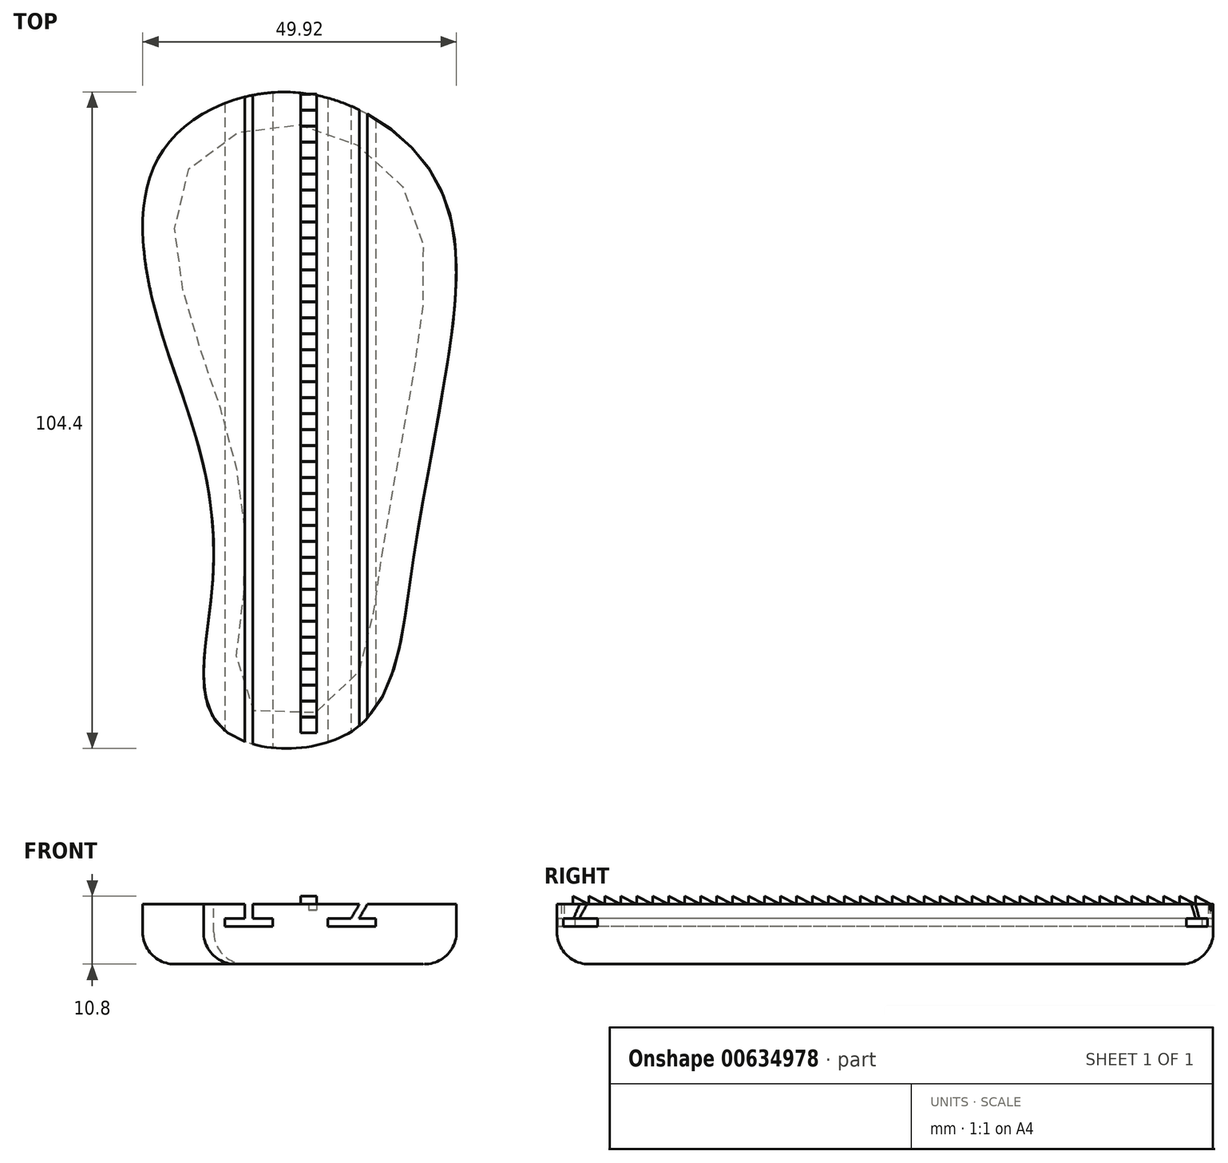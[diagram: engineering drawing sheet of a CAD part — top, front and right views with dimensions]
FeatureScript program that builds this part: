
annotation { "Feature Type Name" : "Feature", "Feature Type Description" : "" }
export const myFeature = defineFeature(function(context is Context, id is Id, definition is map)
    precondition{}
    {
        {
            var Q0;
            Q0=qCreatedBy(makeId("Top.planeOp"),FACE);
            var sketch = newSketch(context, id + "F0", { "sketchPlane" : qUnion([Q0])});
            skFitSpline(sketch, "E0", {"points": [v(-19.82, 9.13) * mm, v(-18.34, 32.17) * mm, v(3.23, 41.76) * mm, v(25.53, 27.56) * mm, v(27.38, 0) * mm, v(21.48, -34.38) * mm, v(12.26, -59.64) * mm, v(-9.13, -58.9) * mm, v(-10.23, -37.15) * mm, v(-12.63, -13.73) * mm, v(-19.82, 9.13) * mm]});
            skSolve(sketch);
        }
        {
            var Q0;
            Q0=makeQuery(id+"F0.imprint","IMPRINT",FACE,{"disambiguationData":[TD([[makeQuery(id+"F0.imprint","IMPRINT",EDGE,{"derivedFrom":sQuery(id+"F0.wireOp",EDGE,"E0")}),-1.0]])]});
            extrude(context, id + "F1", {"entities" : qUnion([Q0]), "depth" : 9.52 * mm, "offsetDistance" : 25.4 * mm});
        }
        {
            var Q0;
            Q0=makeQuery(id+"F1.opExtrude","CAP_EDGE",EDGE,{"disambiguationData":[OSD([sQuery(id+"F0.wireOp",EDGE,"E0")])],"isStart":true});
            fillet(context, id + "F2", {"entities" : qUnion([Q0]), "radius" : 5.08 * mm, "tangentPropagation" : true, "allowEdgeOverflow" : false});
        }
        {
            var Q0;
            Q0=qCreatedBy(makeId("Front.planeOp"),FACE);
            var sketch = newSketch(context, id + "F3", { "sketchPlane" : qUnion([Q0])});
            skLineSegment(sketch, "E1.bottom", {"start": v(8.16, 7.27) * mm, "end": v(11.85, 7.27) * mm});
            skLineSegment(sketch, "E1.top", {"start": v(8.16, 6) * mm, "end": v(15.78, 6) * mm});
            skLineSegment(sketch, "E1.left", {"start": v(8.16, 7.27) * mm, "end": v(8.16, 6) * mm});
            skLineSegment(sketch, "E1.right", {"start": v(15.78, 7.27) * mm, "end": v(15.78, 6) * mm});
            skLineSegment(sketch, "E2.bottom", {"start": v(15.73, 13.84) * mm, "end": v(17, 13.84) * mm});
            skLineSegment(sketch, "E2.left", {"start": v(15.73, 13.84) * mm, "end": v(11.85, 7.27) * mm});
            skLineSegment(sketch, "E2.right", {"start": v(17, 13.84) * mm, "end": v(13.12, 7.27) * mm});
            skLineSegment(sketch, "E3.bottom", {"start": v(-8.2, 6) * mm, "end": v(-0.59, 6) * mm});
            skLineSegment(sketch, "E3.top", {"start": v(-8.2, 7.27) * mm, "end": v(-5.06, 7.27) * mm});
            skLineSegment(sketch, "E3.left", {"start": v(-8.2, 6) * mm, "end": v(-8.2, 7.27) * mm});
            skLineSegment(sketch, "E3.right", {"start": v(-0.59, 6) * mm, "end": v(-0.59, 7.27) * mm});
            skLineSegment(sketch, "E4.bottom", {"start": v(-5.06, 13.84) * mm, "end": v(-3.79, 13.84) * mm});
            skLineSegment(sketch, "E4.left", {"start": v(-5.06, 13.84) * mm, "end": v(-5.06, 7.27) * mm});
            skLineSegment(sketch, "E4.right", {"start": v(-3.79, 13.84) * mm, "end": v(-3.79, 7.27) * mm});
            skLineSegment(sketch, "E5.trimOffspring", {"start": v(-3.79, 7.27) * mm, "end": v(-0.59, 7.27) * mm});
            skLineSegment(sketch, "E6.trimOffspring", {"start": v(13.12, 7.27) * mm, "end": v(15.78, 7.27) * mm});
            skSolve(sketch);
        }
        {
            var Q0;
            Q0=makeQuery(id+"F3.imprint","IMPRINT",FACE,{"disambiguationData":[TD([[makeQuery(id+"F3.imprint","IMPRINT",EDGE,{"derivedFrom":sQuery(id+"F3.wireOp",EDGE,"E3.bottom")}),1.0]])]});
            var Q1;
            Q1=makeQuery(id+"F3.imprint","IMPRINT",FACE,{"disambiguationData":[TD([[makeQuery(id+"F3.imprint","IMPRINT",EDGE,{"derivedFrom":sQuery(id+"F3.wireOp",EDGE,"E1.bottom")}),-1.0]])]});
            extrude(context, id + "F4", {"entities" : qUnion([Q0, Q1]), "operationType" : NewBodyOperationType.REMOVE, "endBound" : BoundingType.THROUGH_ALL, "oppositeDirection" : true, "depth" : 25.4 * mm, "offsetDistance" : 25.4 * mm, "hasSecondDirection" : true, "secondDirectionBound" : SecondDirectionBoundingType.THROUGH_ALL, "secondDirectionOppositeDirection" : false, "secondDirectionDepth" : 25.4 * mm});
        }
        {
            var Q0;
            Q0=qCreatedBy(makeId("Right.planeOp"),FACE);
            cPlane(context, id + "F5", {"entities" : qUnion([Q0]), "cplaneType" : CPlaneType.OFFSET, "offset" : 5.08 * mm, "width" : 152.4 * mm, "height" : 152.4 * mm});
        }
        {
            var Q0;
            Q0=qCreatedBy(id+"F5.planeOp",FACE);
            var sketch = newSketch(context, id + "F6", { "sketchPlane" : qUnion([Q0])});
            skLineSegment(sketch, "E7", {"start": v(41.54, 9.5) * mm, "end": v(39, 10.8) * mm});
            skLineSegment(sketch, "E8", {"start": v(39, 10.8) * mm, "end": v(39, 9.53) * mm});
            skLineSegment(sketch, "E9", {"start": v(41.54, 9.5) * mm, "end": v(41.54, 8.6) * mm});
            skLineSegment(sketch, "E10", {"start": v(41.54, 8.6) * mm, "end": v(38.99, 8.6) * mm});
            skLineSegment(sketch, "E11", {"start": v(38.99, 8.6) * mm, "end": v(39, 9.53) * mm});
            skLineSegment(sketch, "E12.1.0.0", {"start": v(39, 9.5) * mm, "end": v(36.46, 10.8) * mm});
            skLineSegment(sketch, "E12.1.0.1", {"start": v(36.46, 10.8) * mm, "end": v(36.46, 9.53) * mm});
            skLineSegment(sketch, "E12.1.0.2", {"start": v(36.45, 8.6) * mm, "end": v(36.46, 9.53) * mm});
            skLineSegment(sketch, "E12.1.0.3", {"start": v(39, 8.6) * mm, "end": v(36.45, 8.6) * mm});
            skLineSegment(sketch, "E12.1.0.4", {"start": v(39, 9.5) * mm, "end": v(39, 8.6) * mm});
            skLineSegment(sketch, "E12.2.0.0", {"start": v(36.46, 9.5) * mm, "end": v(33.92, 10.8) * mm});
            skLineSegment(sketch, "E12.2.0.1", {"start": v(33.92, 10.8) * mm, "end": v(33.92, 9.53) * mm});
            skLineSegment(sketch, "E12.2.0.2", {"start": v(33.9, 8.6) * mm, "end": v(33.92, 9.53) * mm});
            skLineSegment(sketch, "E12.2.0.3", {"start": v(36.46, 8.6) * mm, "end": v(33.9, 8.6) * mm});
            skLineSegment(sketch, "E12.2.0.4", {"start": v(36.46, 9.5) * mm, "end": v(36.46, 8.6) * mm});
            skLineSegment(sketch, "E12.3.0.0", {"start": v(33.92, 9.5) * mm, "end": v(31.38, 10.8) * mm});
            skLineSegment(sketch, "E12.3.0.1", {"start": v(31.38, 10.8) * mm, "end": v(31.38, 9.53) * mm});
            skLineSegment(sketch, "E12.3.0.2", {"start": v(31.37, 8.6) * mm, "end": v(31.38, 9.53) * mm});
            skLineSegment(sketch, "E12.3.0.3", {"start": v(33.92, 8.6) * mm, "end": v(31.37, 8.6) * mm});
            skLineSegment(sketch, "E12.3.0.4", {"start": v(33.92, 9.5) * mm, "end": v(33.92, 8.6) * mm});
            skLineSegment(sketch, "E12.4.0.0", {"start": v(31.38, 9.5) * mm, "end": v(28.84, 10.8) * mm});
            skLineSegment(sketch, "E12.4.0.1", {"start": v(28.84, 10.8) * mm, "end": v(28.84, 9.53) * mm});
            skLineSegment(sketch, "E12.4.0.2", {"start": v(28.83, 8.6) * mm, "end": v(28.84, 9.53) * mm});
            skLineSegment(sketch, "E12.4.0.3", {"start": v(31.38, 8.6) * mm, "end": v(28.83, 8.6) * mm});
            skLineSegment(sketch, "E12.4.0.4", {"start": v(31.38, 9.5) * mm, "end": v(31.38, 8.6) * mm});
            skLineSegment(sketch, "E12.5.0.0", {"start": v(28.84, 9.5) * mm, "end": v(26.3, 10.8) * mm});
            skLineSegment(sketch, "E12.5.0.1", {"start": v(26.3, 10.8) * mm, "end": v(26.3, 9.53) * mm});
            skLineSegment(sketch, "E12.5.0.2", {"start": v(26.29, 8.6) * mm, "end": v(26.3, 9.53) * mm});
            skLineSegment(sketch, "E12.5.0.3", {"start": v(28.84, 8.6) * mm, "end": v(26.29, 8.6) * mm});
            skLineSegment(sketch, "E12.5.0.4", {"start": v(28.84, 9.5) * mm, "end": v(28.84, 8.6) * mm});
            skLineSegment(sketch, "E12.6.0.0", {"start": v(26.3, 9.5) * mm, "end": v(23.76, 10.8) * mm});
            skLineSegment(sketch, "E12.6.0.1", {"start": v(23.76, 10.8) * mm, "end": v(23.76, 9.53) * mm});
            skLineSegment(sketch, "E12.6.0.2", {"start": v(23.75, 8.6) * mm, "end": v(23.76, 9.53) * mm});
            skLineSegment(sketch, "E12.6.0.3", {"start": v(26.3, 8.6) * mm, "end": v(23.75, 8.6) * mm});
            skLineSegment(sketch, "E12.6.0.4", {"start": v(26.3, 9.5) * mm, "end": v(26.3, 8.6) * mm});
            skLineSegment(sketch, "E12.7.0.0", {"start": v(23.76, 9.5) * mm, "end": v(21.22, 10.8) * mm});
            skLineSegment(sketch, "E12.7.0.1", {"start": v(21.22, 10.8) * mm, "end": v(21.22, 9.53) * mm});
            skLineSegment(sketch, "E12.7.0.2", {"start": v(21.2, 8.6) * mm, "end": v(21.22, 9.53) * mm});
            skLineSegment(sketch, "E12.7.0.3", {"start": v(23.76, 8.6) * mm, "end": v(21.2, 8.6) * mm});
            skLineSegment(sketch, "E12.7.0.4", {"start": v(23.76, 9.5) * mm, "end": v(23.76, 8.6) * mm});
            skLineSegment(sketch, "E12.8.0.0", {"start": v(21.22, 9.5) * mm, "end": v(18.68, 10.8) * mm});
            skLineSegment(sketch, "E12.8.0.1", {"start": v(18.68, 10.8) * mm, "end": v(18.68, 9.53) * mm});
            skLineSegment(sketch, "E12.8.0.2", {"start": v(18.67, 8.6) * mm, "end": v(18.68, 9.53) * mm});
            skLineSegment(sketch, "E12.8.0.3", {"start": v(21.22, 8.6) * mm, "end": v(18.67, 8.6) * mm});
            skLineSegment(sketch, "E12.8.0.4", {"start": v(21.22, 9.5) * mm, "end": v(21.22, 8.6) * mm});
            skLineSegment(sketch, "E12.9.0.0", {"start": v(18.68, 9.5) * mm, "end": v(16.14, 10.8) * mm});
            skLineSegment(sketch, "E12.9.0.1", {"start": v(16.14, 10.8) * mm, "end": v(16.14, 9.53) * mm});
            skLineSegment(sketch, "E12.9.0.2", {"start": v(16.13, 8.6) * mm, "end": v(16.14, 9.53) * mm});
            skLineSegment(sketch, "E12.9.0.3", {"start": v(18.68, 8.6) * mm, "end": v(16.13, 8.6) * mm});
            skLineSegment(sketch, "E12.9.0.4", {"start": v(18.68, 9.5) * mm, "end": v(18.68, 8.6) * mm});
            skLineSegment(sketch, "E12.10.0.0", {"start": v(16.14, 9.5) * mm, "end": v(13.6, 10.8) * mm});
            skLineSegment(sketch, "E12.10.0.1", {"start": v(13.6, 10.8) * mm, "end": v(13.6, 9.53) * mm});
            skLineSegment(sketch, "E12.10.0.2", {"start": v(13.59, 8.6) * mm, "end": v(13.6, 9.53) * mm});
            skLineSegment(sketch, "E12.10.0.3", {"start": v(16.14, 8.6) * mm, "end": v(13.59, 8.6) * mm});
            skLineSegment(sketch, "E12.10.0.4", {"start": v(16.14, 9.5) * mm, "end": v(16.14, 8.6) * mm});
            skLineSegment(sketch, "E12.11.0.0", {"start": v(13.6, 9.5) * mm, "end": v(11.06, 10.8) * mm});
            skLineSegment(sketch, "E12.11.0.1", {"start": v(11.06, 10.8) * mm, "end": v(11.06, 9.53) * mm});
            skLineSegment(sketch, "E12.11.0.2", {"start": v(11.05, 8.6) * mm, "end": v(11.06, 9.53) * mm});
            skLineSegment(sketch, "E12.11.0.3", {"start": v(13.6, 8.6) * mm, "end": v(11.05, 8.6) * mm});
            skLineSegment(sketch, "E12.11.0.4", {"start": v(13.6, 9.5) * mm, "end": v(13.6, 8.6) * mm});
            skLineSegment(sketch, "E12.12.0.0", {"start": v(11.06, 9.5) * mm, "end": v(8.52, 10.8) * mm});
            skLineSegment(sketch, "E12.12.0.1", {"start": v(8.52, 10.8) * mm, "end": v(8.52, 9.53) * mm});
            skLineSegment(sketch, "E12.12.0.2", {"start": v(8.5, 8.6) * mm, "end": v(8.52, 9.53) * mm});
            skLineSegment(sketch, "E12.12.0.3", {"start": v(11.06, 8.6) * mm, "end": v(8.5, 8.6) * mm});
            skLineSegment(sketch, "E12.12.0.4", {"start": v(11.06, 9.5) * mm, "end": v(11.06, 8.6) * mm});
            skLineSegment(sketch, "E12.13.0.0", {"start": v(8.52, 9.5) * mm, "end": v(5.98, 10.8) * mm});
            skLineSegment(sketch, "E12.13.0.1", {"start": v(5.98, 10.8) * mm, "end": v(5.98, 9.53) * mm});
            skLineSegment(sketch, "E12.13.0.2", {"start": v(5.97, 8.6) * mm, "end": v(5.98, 9.53) * mm});
            skLineSegment(sketch, "E12.13.0.3", {"start": v(8.52, 8.6) * mm, "end": v(5.97, 8.6) * mm});
            skLineSegment(sketch, "E12.13.0.4", {"start": v(8.52, 9.5) * mm, "end": v(8.52, 8.6) * mm});
            skLineSegment(sketch, "E12.14.0.0", {"start": v(5.98, 9.5) * mm, "end": v(3.44, 10.8) * mm});
            skLineSegment(sketch, "E12.14.0.1", {"start": v(3.44, 10.8) * mm, "end": v(3.44, 9.53) * mm});
            skLineSegment(sketch, "E12.14.0.2", {"start": v(3.43, 8.6) * mm, "end": v(3.44, 9.53) * mm});
            skLineSegment(sketch, "E12.14.0.3", {"start": v(5.98, 8.6) * mm, "end": v(3.43, 8.6) * mm});
            skLineSegment(sketch, "E12.14.0.4", {"start": v(5.98, 9.5) * mm, "end": v(5.98, 8.6) * mm});
            skLineSegment(sketch, "E12.15.0.0", {"start": v(3.44, 9.5) * mm, "end": v(0.9, 10.8) * mm});
            skLineSegment(sketch, "E12.15.0.1", {"start": v(0.9, 10.8) * mm, "end": v(0.9, 9.53) * mm});
            skLineSegment(sketch, "E12.15.0.2", {"start": v(0.89, 8.6) * mm, "end": v(0.9, 9.53) * mm});
            skLineSegment(sketch, "E12.15.0.3", {"start": v(3.44, 8.6) * mm, "end": v(0.89, 8.6) * mm});
            skLineSegment(sketch, "E12.15.0.4", {"start": v(3.44, 9.5) * mm, "end": v(3.44, 8.6) * mm});
            skLineSegment(sketch, "E12.16.0.0", {"start": v(0.9, 9.5) * mm, "end": v(-1.64, 10.8) * mm});
            skLineSegment(sketch, "E12.16.0.1", {"start": v(-1.64, 10.8) * mm, "end": v(-1.64, 9.53) * mm});
            skLineSegment(sketch, "E12.16.0.2", {"start": v(-1.65, 8.6) * mm, "end": v(-1.64, 9.53) * mm});
            skLineSegment(sketch, "E12.16.0.3", {"start": v(0.9, 8.6) * mm, "end": v(-1.65, 8.6) * mm});
            skLineSegment(sketch, "E12.16.0.4", {"start": v(0.9, 9.5) * mm, "end": v(0.9, 8.6) * mm});
            skLineSegment(sketch, "E12.17.0.0", {"start": v(-1.64, 9.5) * mm, "end": v(-4.18, 10.8) * mm});
            skLineSegment(sketch, "E12.17.0.1", {"start": v(-4.18, 10.8) * mm, "end": v(-4.18, 9.53) * mm});
            skLineSegment(sketch, "E12.17.0.2", {"start": v(-4.2, 8.6) * mm, "end": v(-4.18, 9.53) * mm});
            skLineSegment(sketch, "E12.17.0.3", {"start": v(-1.64, 8.6) * mm, "end": v(-4.2, 8.6) * mm});
            skLineSegment(sketch, "E12.17.0.4", {"start": v(-1.64, 9.5) * mm, "end": v(-1.64, 8.6) * mm});
            skLineSegment(sketch, "E12.18.0.0", {"start": v(-4.18, 9.5) * mm, "end": v(-6.72, 10.8) * mm});
            skLineSegment(sketch, "E12.18.0.1", {"start": v(-6.72, 10.8) * mm, "end": v(-6.72, 9.53) * mm});
            skLineSegment(sketch, "E12.18.0.2", {"start": v(-6.73, 8.6) * mm, "end": v(-6.72, 9.53) * mm});
            skLineSegment(sketch, "E12.18.0.3", {"start": v(-4.18, 8.6) * mm, "end": v(-6.73, 8.6) * mm});
            skLineSegment(sketch, "E12.18.0.4", {"start": v(-4.18, 9.5) * mm, "end": v(-4.18, 8.6) * mm});
            skLineSegment(sketch, "E12.19.0.0", {"start": v(-6.72, 9.5) * mm, "end": v(-9.26, 10.8) * mm});
            skLineSegment(sketch, "E12.19.0.1", {"start": v(-9.26, 10.8) * mm, "end": v(-9.26, 9.53) * mm});
            skLineSegment(sketch, "E12.19.0.2", {"start": v(-9.27, 8.6) * mm, "end": v(-9.26, 9.53) * mm});
            skLineSegment(sketch, "E12.19.0.3", {"start": v(-6.72, 8.6) * mm, "end": v(-9.27, 8.6) * mm});
            skLineSegment(sketch, "E12.19.0.4", {"start": v(-6.72, 9.5) * mm, "end": v(-6.72, 8.6) * mm});
            skLineSegment(sketch, "E12.20.0.0", {"start": v(-9.26, 9.5) * mm, "end": v(-11.8, 10.8) * mm});
            skLineSegment(sketch, "E12.20.0.1", {"start": v(-11.8, 10.8) * mm, "end": v(-11.8, 9.53) * mm});
            skLineSegment(sketch, "E12.20.0.2", {"start": v(-11.81, 8.6) * mm, "end": v(-11.8, 9.53) * mm});
            skLineSegment(sketch, "E12.20.0.3", {"start": v(-9.26, 8.6) * mm, "end": v(-11.81, 8.6) * mm});
            skLineSegment(sketch, "E12.20.0.4", {"start": v(-9.26, 9.5) * mm, "end": v(-9.26, 8.6) * mm});
            skLineSegment(sketch, "E12.21.0.0", {"start": v(-11.8, 9.5) * mm, "end": v(-14.34, 10.8) * mm});
            skLineSegment(sketch, "E12.21.0.1", {"start": v(-14.34, 10.8) * mm, "end": v(-14.34, 9.53) * mm});
            skLineSegment(sketch, "E12.21.0.2", {"start": v(-14.35, 8.6) * mm, "end": v(-14.34, 9.53) * mm});
            skLineSegment(sketch, "E12.21.0.3", {"start": v(-11.8, 8.6) * mm, "end": v(-14.35, 8.6) * mm});
            skLineSegment(sketch, "E12.21.0.4", {"start": v(-11.8, 9.5) * mm, "end": v(-11.8, 8.6) * mm});
            skLineSegment(sketch, "E12.22.0.0", {"start": v(-14.34, 9.5) * mm, "end": v(-16.88, 10.8) * mm});
            skLineSegment(sketch, "E12.22.0.1", {"start": v(-16.88, 10.8) * mm, "end": v(-16.88, 9.53) * mm});
            skLineSegment(sketch, "E12.22.0.2", {"start": v(-16.9, 8.6) * mm, "end": v(-16.88, 9.53) * mm});
            skLineSegment(sketch, "E12.22.0.3", {"start": v(-14.34, 8.6) * mm, "end": v(-16.9, 8.6) * mm});
            skLineSegment(sketch, "E12.22.0.4", {"start": v(-14.34, 9.5) * mm, "end": v(-14.34, 8.6) * mm});
            skLineSegment(sketch, "E12.23.0.0", {"start": v(-16.88, 9.5) * mm, "end": v(-19.42, 10.8) * mm});
            skLineSegment(sketch, "E12.23.0.1", {"start": v(-19.42, 10.8) * mm, "end": v(-19.42, 9.53) * mm});
            skLineSegment(sketch, "E12.23.0.2", {"start": v(-19.43, 8.6) * mm, "end": v(-19.42, 9.53) * mm});
            skLineSegment(sketch, "E12.23.0.3", {"start": v(-16.88, 8.6) * mm, "end": v(-19.43, 8.6) * mm});
            skLineSegment(sketch, "E12.23.0.4", {"start": v(-16.88, 9.5) * mm, "end": v(-16.88, 8.6) * mm});
            skLineSegment(sketch, "E12.24.0.0", {"start": v(-19.42, 9.5) * mm, "end": v(-21.96, 10.8) * mm});
            skLineSegment(sketch, "E12.24.0.1", {"start": v(-21.96, 10.8) * mm, "end": v(-21.96, 9.53) * mm});
            skLineSegment(sketch, "E12.24.0.2", {"start": v(-21.97, 8.6) * mm, "end": v(-21.96, 9.53) * mm});
            skLineSegment(sketch, "E12.24.0.3", {"start": v(-19.42, 8.6) * mm, "end": v(-21.97, 8.6) * mm});
            skLineSegment(sketch, "E12.24.0.4", {"start": v(-19.42, 9.5) * mm, "end": v(-19.42, 8.6) * mm});
            skLineSegment(sketch, "E12.25.0.0", {"start": v(-21.96, 9.5) * mm, "end": v(-24.5, 10.8) * mm});
            skLineSegment(sketch, "E12.25.0.1", {"start": v(-24.5, 10.8) * mm, "end": v(-24.5, 9.53) * mm});
            skLineSegment(sketch, "E12.25.0.2", {"start": v(-24.51, 8.6) * mm, "end": v(-24.5, 9.53) * mm});
            skLineSegment(sketch, "E12.25.0.3", {"start": v(-21.96, 8.6) * mm, "end": v(-24.51, 8.6) * mm});
            skLineSegment(sketch, "E12.25.0.4", {"start": v(-21.96, 9.5) * mm, "end": v(-21.96, 8.6) * mm});
            skLineSegment(sketch, "E12.26.0.0", {"start": v(-24.5, 9.5) * mm, "end": v(-27.04, 10.8) * mm});
            skLineSegment(sketch, "E12.26.0.1", {"start": v(-27.04, 10.8) * mm, "end": v(-27.04, 9.53) * mm});
            skLineSegment(sketch, "E12.26.0.2", {"start": v(-27.05, 8.6) * mm, "end": v(-27.04, 9.53) * mm});
            skLineSegment(sketch, "E12.26.0.3", {"start": v(-24.5, 8.6) * mm, "end": v(-27.05, 8.6) * mm});
            skLineSegment(sketch, "E12.26.0.4", {"start": v(-24.5, 9.5) * mm, "end": v(-24.5, 8.6) * mm});
            skLineSegment(sketch, "E12.27.0.0", {"start": v(-27.04, 9.5) * mm, "end": v(-29.58, 10.8) * mm});
            skLineSegment(sketch, "E12.27.0.1", {"start": v(-29.58, 10.8) * mm, "end": v(-29.58, 9.53) * mm});
            skLineSegment(sketch, "E12.27.0.2", {"start": v(-29.6, 8.6) * mm, "end": v(-29.58, 9.53) * mm});
            skLineSegment(sketch, "E12.27.0.3", {"start": v(-27.04, 8.6) * mm, "end": v(-29.6, 8.6) * mm});
            skLineSegment(sketch, "E12.27.0.4", {"start": v(-27.04, 9.5) * mm, "end": v(-27.04, 8.6) * mm});
            skLineSegment(sketch, "E12.28.0.0", {"start": v(-29.58, 9.5) * mm, "end": v(-32.12, 10.8) * mm});
            skLineSegment(sketch, "E12.28.0.1", {"start": v(-32.12, 10.8) * mm, "end": v(-32.12, 9.53) * mm});
            skLineSegment(sketch, "E12.28.0.2", {"start": v(-32.13, 8.6) * mm, "end": v(-32.12, 9.53) * mm});
            skLineSegment(sketch, "E12.28.0.3", {"start": v(-29.58, 8.6) * mm, "end": v(-32.13, 8.6) * mm});
            skLineSegment(sketch, "E12.28.0.4", {"start": v(-29.58, 9.5) * mm, "end": v(-29.58, 8.6) * mm});
            skLineSegment(sketch, "E12.29.0.0", {"start": v(-32.12, 9.5) * mm, "end": v(-34.66, 10.8) * mm});
            skLineSegment(sketch, "E12.29.0.1", {"start": v(-34.66, 10.8) * mm, "end": v(-34.66, 9.53) * mm});
            skLineSegment(sketch, "E12.29.0.2", {"start": v(-34.67, 8.6) * mm, "end": v(-34.66, 9.53) * mm});
            skLineSegment(sketch, "E12.29.0.3", {"start": v(-32.12, 8.6) * mm, "end": v(-34.67, 8.6) * mm});
            skLineSegment(sketch, "E12.29.0.4", {"start": v(-32.12, 9.5) * mm, "end": v(-32.12, 8.6) * mm});
            skLineSegment(sketch, "E12.30.0.0", {"start": v(-34.66, 9.5) * mm, "end": v(-37.2, 10.8) * mm});
            skLineSegment(sketch, "E12.30.0.1", {"start": v(-37.2, 10.8) * mm, "end": v(-37.2, 9.53) * mm});
            skLineSegment(sketch, "E12.30.0.2", {"start": v(-37.21, 8.6) * mm, "end": v(-37.2, 9.53) * mm});
            skLineSegment(sketch, "E12.30.0.3", {"start": v(-34.66, 8.6) * mm, "end": v(-37.21, 8.6) * mm});
            skLineSegment(sketch, "E12.30.0.4", {"start": v(-34.66, 9.5) * mm, "end": v(-34.66, 8.6) * mm});
            skLineSegment(sketch, "E12.31.0.0", {"start": v(-37.2, 9.5) * mm, "end": v(-39.74, 10.8) * mm});
            skLineSegment(sketch, "E12.31.0.1", {"start": v(-39.74, 10.8) * mm, "end": v(-39.74, 9.53) * mm});
            skLineSegment(sketch, "E12.31.0.2", {"start": v(-39.75, 8.6) * mm, "end": v(-39.74, 9.53) * mm});
            skLineSegment(sketch, "E12.31.0.3", {"start": v(-37.2, 8.6) * mm, "end": v(-39.75, 8.6) * mm});
            skLineSegment(sketch, "E12.31.0.4", {"start": v(-37.2, 9.5) * mm, "end": v(-37.2, 8.6) * mm});
            skLineSegment(sketch, "E12.32.0.0", {"start": v(-39.74, 9.5) * mm, "end": v(-42.28, 10.8) * mm});
            skLineSegment(sketch, "E12.32.0.1", {"start": v(-42.28, 10.8) * mm, "end": v(-42.28, 9.53) * mm});
            skLineSegment(sketch, "E12.32.0.2", {"start": v(-42.3, 8.6) * mm, "end": v(-42.28, 9.53) * mm});
            skLineSegment(sketch, "E12.32.0.3", {"start": v(-39.74, 8.6) * mm, "end": v(-42.3, 8.6) * mm});
            skLineSegment(sketch, "E12.32.0.4", {"start": v(-39.74, 9.5) * mm, "end": v(-39.74, 8.6) * mm});
            skLineSegment(sketch, "E12.33.0.0", {"start": v(-42.28, 9.5) * mm, "end": v(-44.82, 10.8) * mm});
            skLineSegment(sketch, "E12.33.0.1", {"start": v(-44.82, 10.8) * mm, "end": v(-44.82, 9.53) * mm});
            skLineSegment(sketch, "E12.33.0.2", {"start": v(-44.83, 8.6) * mm, "end": v(-44.82, 9.53) * mm});
            skLineSegment(sketch, "E12.33.0.3", {"start": v(-42.28, 8.6) * mm, "end": v(-44.83, 8.6) * mm});
            skLineSegment(sketch, "E12.33.0.4", {"start": v(-42.28, 9.5) * mm, "end": v(-42.28, 8.6) * mm});
            skLineSegment(sketch, "E12.34.0.0", {"start": v(-44.82, 9.5) * mm, "end": v(-47.36, 10.8) * mm});
            skLineSegment(sketch, "E12.34.0.1", {"start": v(-47.36, 10.8) * mm, "end": v(-47.36, 9.53) * mm});
            skLineSegment(sketch, "E12.34.0.2", {"start": v(-47.37, 8.6) * mm, "end": v(-47.36, 9.53) * mm});
            skLineSegment(sketch, "E12.34.0.3", {"start": v(-44.82, 8.6) * mm, "end": v(-47.37, 8.6) * mm});
            skLineSegment(sketch, "E12.34.0.4", {"start": v(-44.82, 9.5) * mm, "end": v(-44.82, 8.6) * mm});
            skLineSegment(sketch, "E12.35.0.0", {"start": v(-47.36, 9.5) * mm, "end": v(-49.9, 10.8) * mm});
            skLineSegment(sketch, "E12.35.0.1", {"start": v(-49.9, 10.8) * mm, "end": v(-49.9, 9.53) * mm});
            skLineSegment(sketch, "E12.35.0.2", {"start": v(-49.91, 8.6) * mm, "end": v(-49.9, 9.53) * mm});
            skLineSegment(sketch, "E12.35.0.3", {"start": v(-47.36, 8.6) * mm, "end": v(-49.91, 8.6) * mm});
            skLineSegment(sketch, "E12.35.0.4", {"start": v(-47.36, 9.5) * mm, "end": v(-47.36, 8.6) * mm});
            skLineSegment(sketch, "E12.36.0.0", {"start": v(-49.9, 9.5) * mm, "end": v(-52.44, 10.8) * mm});
            skLineSegment(sketch, "E12.36.0.1", {"start": v(-52.44, 10.8) * mm, "end": v(-52.44, 9.53) * mm});
            skLineSegment(sketch, "E12.36.0.2", {"start": v(-52.45, 8.6) * mm, "end": v(-52.44, 9.53) * mm});
            skLineSegment(sketch, "E12.36.0.3", {"start": v(-49.9, 8.6) * mm, "end": v(-52.45, 8.6) * mm});
            skLineSegment(sketch, "E12.36.0.4", {"start": v(-49.9, 9.5) * mm, "end": v(-49.9, 8.6) * mm});
            skLineSegment(sketch, "E12.37.0.0", {"start": v(-52.44, 9.5) * mm, "end": v(-54.98, 10.8) * mm});
            skLineSegment(sketch, "E12.37.0.1", {"start": v(-54.98, 10.8) * mm, "end": v(-54.98, 9.53) * mm});
            skLineSegment(sketch, "E12.37.0.2", {"start": v(-55, 8.6) * mm, "end": v(-54.98, 9.53) * mm});
            skLineSegment(sketch, "E12.37.0.3", {"start": v(-52.44, 8.6) * mm, "end": v(-55, 8.6) * mm});
            skLineSegment(sketch, "E12.37.0.4", {"start": v(-52.44, 9.5) * mm, "end": v(-52.44, 8.6) * mm});
            skLineSegment(sketch, "E12.38.0.0", {"start": v(-54.98, 9.5) * mm, "end": v(-57.52, 10.8) * mm});
            skLineSegment(sketch, "E12.38.0.1", {"start": v(-57.52, 10.8) * mm, "end": v(-57.52, 9.53) * mm});
            skLineSegment(sketch, "E12.38.0.2", {"start": v(-57.53, 8.6) * mm, "end": v(-57.52, 9.53) * mm});
            skLineSegment(sketch, "E12.38.0.3", {"start": v(-54.98, 8.6) * mm, "end": v(-57.53, 8.6) * mm});
            skLineSegment(sketch, "E12.38.0.4", {"start": v(-54.98, 9.5) * mm, "end": v(-54.98, 8.6) * mm});
            skLineSegment(sketch, "E12.39.0.0", {"start": v(-57.52, 9.5) * mm, "end": v(-60.06, 10.8) * mm});
            skLineSegment(sketch, "E12.39.0.1", {"start": v(-60.06, 10.8) * mm, "end": v(-60.06, 9.53) * mm});
            skLineSegment(sketch, "E12.39.0.2", {"start": v(-60.07, 8.6) * mm, "end": v(-60.06, 9.53) * mm});
            skLineSegment(sketch, "E12.39.0.3", {"start": v(-57.52, 8.6) * mm, "end": v(-60.07, 8.6) * mm});
            skLineSegment(sketch, "E12.39.0.4", {"start": v(-57.52, 9.5) * mm, "end": v(-57.52, 8.6) * mm});
            skLineSegment(sketch, "E12.direction1", {"start": v(39, 10.8) * mm, "end": v(36.46, 10.8) * mm, "construction": true});
            skSolve(sketch);
        }
        {
            var Q0;
            Q0 = qSketchRegion(id + "F6", true);
            extrude(context, id + "F7", {"entities" : qUnion([Q0]), "operationType" : NewBodyOperationType.ADD, "endBound" : BoundingType.SYMMETRIC, "depth" : 2.54 * mm, "offsetDistance" : 25.4 * mm});
        }
    });
